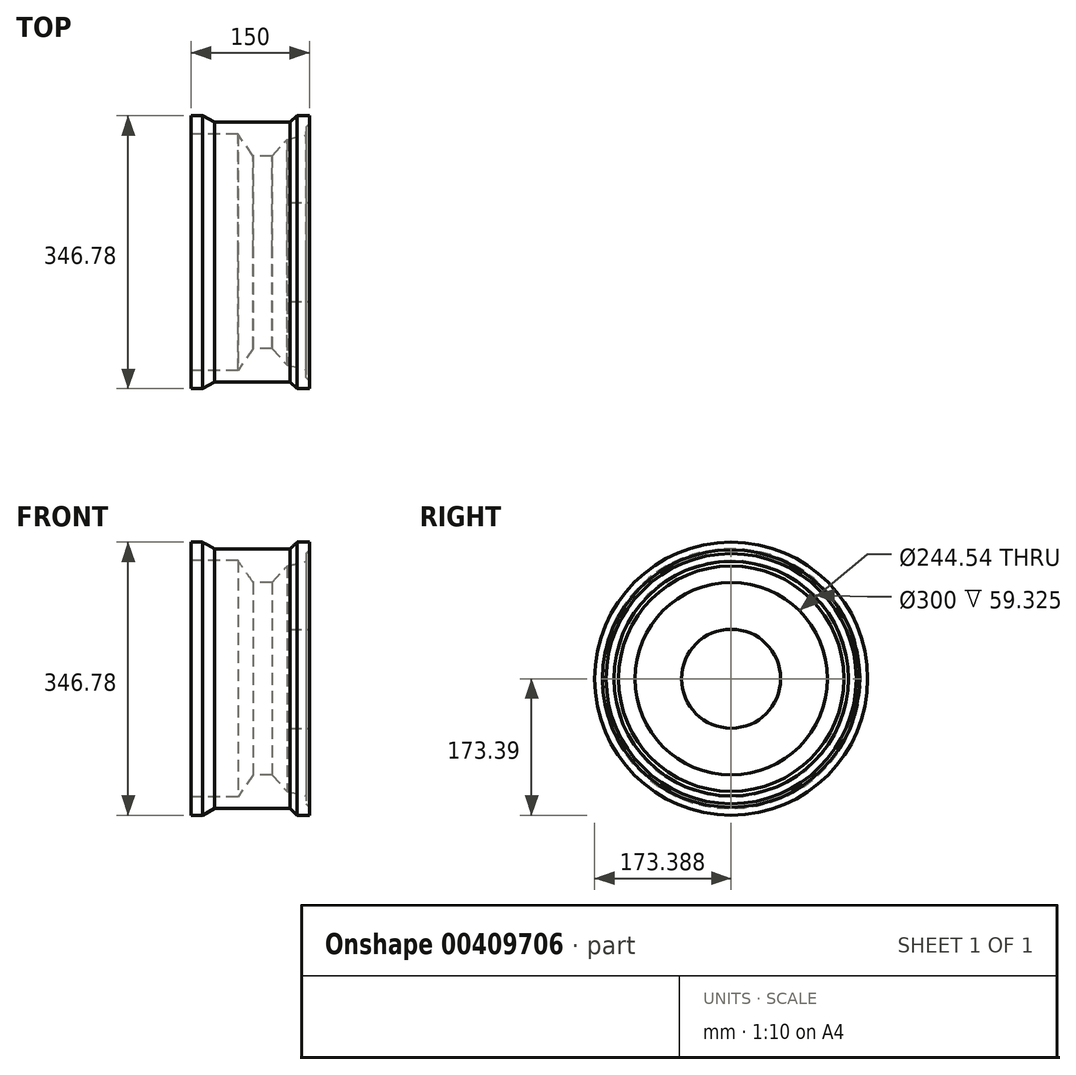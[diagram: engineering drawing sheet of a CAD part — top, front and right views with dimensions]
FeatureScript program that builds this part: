
annotation { "Feature Type Name" : "Feature", "Feature Type Description" : "" }
export const myFeature = defineFeature(function(context is Context, id is Id, definition is map)
    precondition{}
    {
        {
            var Q0;
            Q0=qCreatedBy(makeId("Top.planeOp"),FACE);
            var sketch = newSketch(context, id + "F0", { "sketchPlane" : qUnion([Q0])});
            skLineSegment(sketch, "E0", {"start": v(0, 0) * mm, "end": v(14.56, 0) * mm});
            skLineSegment(sketch, "E1", {"start": v(14.56, 0) * mm, "end": v(29.49, 8.39) * mm});
            skLineSegment(sketch, "E2", {"start": v(29.49, 8.39) * mm, "end": v(125.47, 8.39) * mm});
            skLineSegment(sketch, "E3", {"start": v(125.47, 8.39) * mm, "end": v(134.54, 0) * mm});
            skLineSegment(sketch, "E4", {"start": v(134.54, 0) * mm, "end": v(150, 0) * mm});
            skLineSegment(sketch, "E5", {"start": v(150, 0) * mm, "end": v(150, 10) * mm});
            skLineSegment(sketch, "E6", {"start": v(150, 10) * mm, "end": v(146.05, 14.52) * mm});
            skLineSegment(sketch, "E7", {"start": v(146.05, 14.52) * mm, "end": v(146.05, 24.52) * mm});
            skLineSegment(sketch, "E8", {"start": v(146.05, 24.52) * mm, "end": v(121.71, 30.24) * mm});
            skLineSegment(sketch, "E9", {"start": v(121.71, 30.24) * mm, "end": v(102.52, 51.12) * mm});
            skLineSegment(sketch, "E10", {"start": v(102.52, 51.12) * mm, "end": v(78.52, 51.12) * mm});
            skLineSegment(sketch, "E11", {"start": v(78.52, 51.12) * mm, "end": v(59.33, 23.39) * mm});
            skLineSegment(sketch, "E12", {"start": v(59.33, 23.39) * mm, "end": v(0, 23.39) * mm});
            skLineSegment(sketch, "E13", {"start": v(0, 23.39) * mm, "end": v(0, 0) * mm});
            skSolve(sketch);
        }
        {
            var Q0;
            Q0=makeQuery(id+"F0.imprint","IMPRINT",FACE,{"disambiguationData":[TD([[makeQuery(id+"F0.imprint","IMPRINT",EDGE,{"derivedFrom":sQuery(id+"F0.wireOp",EDGE,"E0")}),1.0]])]});
            var sketch = newSketch(context, id + "F1", { "sketchPlane" : qUnion([Q0])});
            skLineSegment(sketch, "E14", {"start": v(45.7, 173.39) * mm, "end": v(125.26, 173.39) * mm});
            skSolve(sketch);
        }
        {
            var Q0;
            Q0 = qSketchRegion(id + "F0", true);
            var Q1;
            Q1=sQuery(id+"F1.wireOp",EDGE,"E14");
            revolve(context, id + "F2", {"entities" : qUnion([Q0]), "axis" : qUnion([Q1]), "revolveType" : RevolveType.FULL});
        }
        {
            var Q0;
            Q0=makeQuery(id+"F2.opRevolve","SWEPT_FACE",FACE,{"disambiguationData":[OSD([sQuery(id+"F0.wireOp",EDGE,"E5")])]});
            var sketch = newSketch(context, id + "F3", { "sketchPlane" : qUnion([Q0])});
            skPoint(sketch, "E15", {"position": v(173.39, 0) * mm});
            skSolve(sketch);
        }
        {
            var Q0;
            {var subQ0=sQuery(id+"F0.wireOp",EDGE,"E5");Q0=makeQuery(id+"F3.imprint","IMPRINT",FACE,{"disambiguationData":[TD([[makeQuery(id+"F3.imprint","IMPRINT",EDGE,{"derivedFrom":makeQuery(id+"F2.opRevolve","SWEPT_EDGE",EDGE,{"disambiguationData":[OSD([sQuery(id+"F0.wireOp",EDGE,"E4"),subQ0])]})}),-1.0]])]});}
            var sketch = newSketch(context, id + "F4", { "sketchPlane" : qUnion([Q0])});
            skCircle(sketch, "E16", {"center": v(173.37, 0) * mm, "radius": 62.85 * mm});
            skSolve(sketch);
        }
        {
            var Q0;
            Q0 = qSketchRegion(id + "F4", true);
            extrude(context, id + "F5", {"entities" : qUnion([Q0]), "oppositeDirection" : true, "depth" : 25 * mm});
        }
    });
